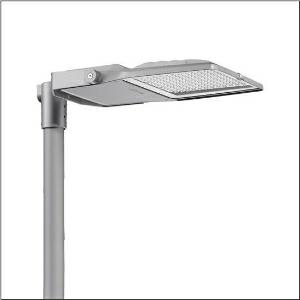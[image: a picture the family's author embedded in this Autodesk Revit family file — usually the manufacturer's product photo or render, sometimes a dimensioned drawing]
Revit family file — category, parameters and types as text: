
# Revit family: floodlight_fl_21_midi___pl43_5xa7785f2a3a_ea2c
name_source: partatom
category: Lighting Fixtures
units: mm (PartAtom-declared; Revit-internal decimal feet)

## family parameters
Cut with Voids When Loaded = No
Host = Face
Light Source = No
Part Type = Normal
Room Calculation Point = No
Round Connector Dimension = Use Diameter
Shared = No

## types (1)
- --- (1 x LED, 36680 lm, 271.6 W, 3000K)
    Apparent Load = 272 VA
    CIE Flux Codes = 27 78 99 100 100
    Color Rendering = 70
    Color Temperature = 3000K
    Default Elevation = 1800 mm
    Description = Floodlight FL 21 midi, floodlight, primary light control with lens, of PMMA, primary optical cover: protective disc, of toughened safety glass, transparent, light distribution: PL43, light emission: direct distribution, installation type: surface-mounted, LED, High Power LED, rated luminous flux: 36.680lm, luminous efficacy: 135lm/W, light colour: 730, colour temperature: 3000K, control gear: Smart Interface (Zhaga), control: flexible luminous flux parameterisation, time-dependent luminous flux control, constant luminous flux control, overheat protection, pre-setting: logarithmic dimming characteristic, with terminal, 6-pole, mains connection: 220..240V, AC, 50/60Hz, start of lifetime: 272W, end of service life: 287W, reduction: 123W, luminaire housing, of diecast aluminium, powder-coated, SITECO metallic grey (DB 702S), corrosivity category C5 mid according to DIN EN ISO 12944, suitable for swimming pools, chlorine-resistant, sealing non-destructively replaceable, please order mast flange separately, mast bracket, of steel, galvanised, powder-coated, SITECO metallic grey (DB 702S), Smart Interface above, protection rating (complete): IP66, insulation class (complete): insulation class II (safety insulation), certification: CE, ENEC, VDE, protection symbol: D, impact resistance: IK08, permissible operating ambient temperature: -40..+40°C, permissible operating ambient temperature for outdoor applications: -40..+50°C, standard: DIN EN 12944, LABS conformity tested according to VDMA 24364:2018-05, packaging unit: 1 piece

Light Distribution: PL43
    Height = 76 mm
    Lamp = 1 x LED
    Lamp Light Flux = 36680 lm
    Lamp Power = 271.6 W
    Lamp count = 1
    Length = 657 mm
    Luminous efficacy = 135 lm/W
    Manufacturer = Siteco
    ModVariant = No
    Model = 5XA7785F2A3A
    Number of Poles = 1
    OnlyDefault = Yes
    Power Factor = 1
    Product Name = Floodlight FL 21 midi | PL43
    Product group = floodlight | pylon annexe
    ProductGroupID = 6201
    Protection Class = Protection class II
    Protection Degree = IP 66
    RLX_Detail_Level = 1
    RLX_Emergency_Light_Flux = 0 lm
    RLX_Emergency_Type = 0
    RLX_Emergency_Type_DB = No
    RlxData = <blob elided: 153545 chars, md5=aec84ae5>
    Socket = socket
    Standby Power = 0 W
    System Light Flux = 36680 lm
    System Power = 272 W
    Type Comments = factory setting: luminous flux: 100 % | dim-lin: 254 | 620 mA
    Type Image = l_1007123.jpg
    URL = http://relux.com
    VarID = @adj_176655
    Voltage = 0 V
    Weight = 0.00 kg
    Width = 442 mm

## geometry (parser evidence)
native form markers: Blend x4, Sweep x12
no freeform markers — native parametric forms only
